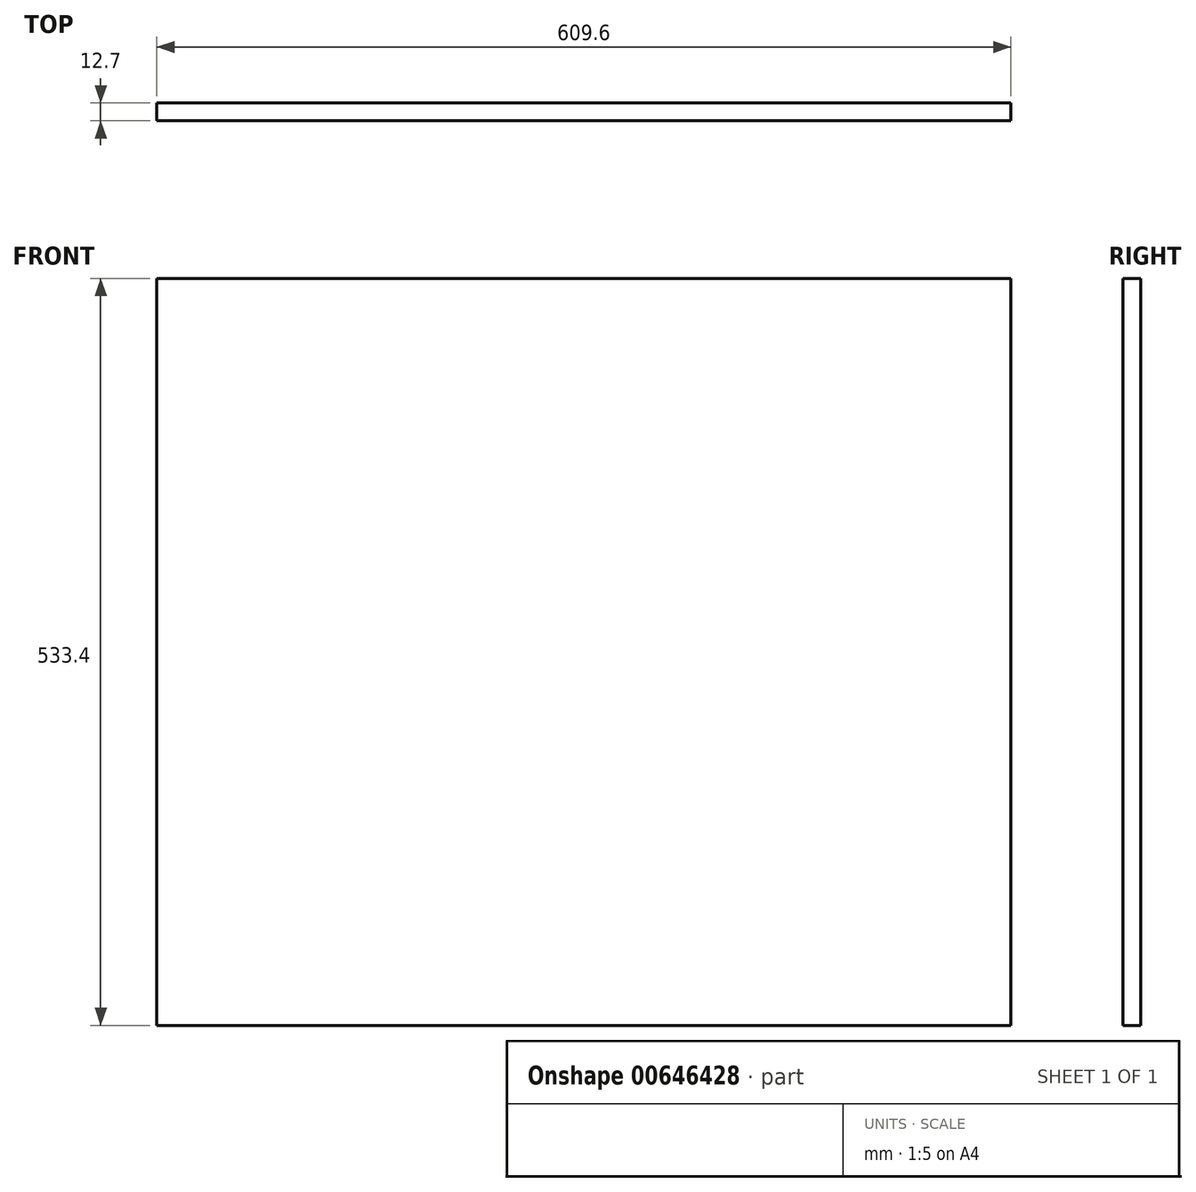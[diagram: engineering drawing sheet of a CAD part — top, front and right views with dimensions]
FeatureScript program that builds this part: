
annotation { "Feature Type Name" : "Feature", "Feature Type Description" : "" }
export const myFeature = defineFeature(function(context is Context, id is Id, definition is map)
    precondition{}
    {
        {
            var Q0;
            Q0=qCreatedBy(makeId("Front.planeOp"),FACE);
            var sketch = newSketch(context, id + "F0", { "sketchPlane" : qUnion([Q0])});
            skLineSegment(sketch, "E0.bottom", {"start": v(304.8, 266.7) * mm, "end": v(-304.8, 266.7) * mm});
            skLineSegment(sketch, "E0.top", {"start": v(304.8, -266.7) * mm, "end": v(-304.8, -266.7) * mm});
            skLineSegment(sketch, "E0.left", {"start": v(304.8, 266.7) * mm, "end": v(304.8, -266.7) * mm});
            skLineSegment(sketch, "E0.right", {"start": v(-304.8, 266.7) * mm, "end": v(-304.8, -266.7) * mm});
            skPoint(sketch, "E0.middle", {"position": v(0, 0) * mm});
            skSolve(sketch);
        }
        {
            var Q0;
            Q0 = qSketchRegion(id + "F0", true);
            extrude(context, id + "F1", {"entities" : qUnion([Q0]), "depth" : 12.7 * mm, "offsetDistance" : 25.4 * mm});
        }
    });
